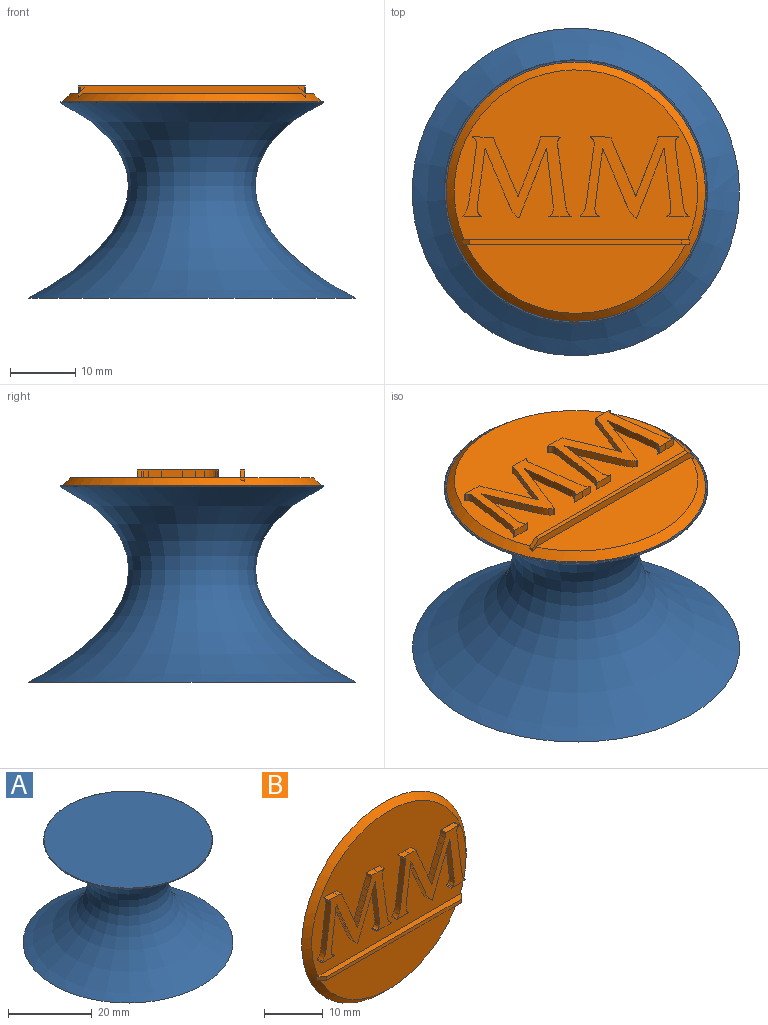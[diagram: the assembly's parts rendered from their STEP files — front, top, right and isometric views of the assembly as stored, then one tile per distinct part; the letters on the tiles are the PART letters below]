
ASSEMBLY  parts=2 mates=1
PART A: 4 faces, bbox 50x50x30 mm
  f0: plane 40.08x40.08mm, normal (0,0,1), area 1261.5mm2, adj f1
  f1: torus R=20.04mm, axis (0,0,1), area 34.2mm2, adj f0
  f2: plane 50x50mm, normal (0,0,-1), area 1963.5mm2, adj f3
  f3: revolved ~50x50mm, area 7734.9mm2, adj f2
PART B: 167 faces, bbox 39.6x2.4x39.6 mm
  f0: plane 37.2x25.95mm, normal (0,-1,0), area 657.2mm2, adj f3,f4,f5,f6,f7,f8,f9,f10
  f1: plane 33.53x10.54mm, normal (0,-1,0), area 253.3mm2, adj f160,f164
  f2: plane 39.6x39.6mm, normal (0,1,0), area 1231.6mm2, adj f164
  f3: plane 1.2x0.09mm, normal (0.59,0,-0.81), area 0.1mm2, adj f0,f4,f88,f89
  f4: extruded ~1.2x0.21mm, area 0.3mm2, adj f0,f3,f5,f89
  f5: extruded ~1.2x1.18mm, area 1.5mm2, adj f0,f4,f6,f89
  f6: extruded ~1.22x1.2mm, area 1.6mm2, adj f0,f5,f7,f89
  f7: extruded ~1.2x0.87mm, area 1.1mm2, adj f0,f6,f8,f89
  f8: extruded ~1.2x1mm, area 1.3mm2, adj f0,f7,f9,f89
  f9: extruded ~1.21x1.2mm, area 1.6mm2, adj f0,f8,f10,f89
  f10: extruded ~2.99x1.2mm, area 3.8mm2, adj f0,f9,f11,f89
  f11: extruded ~1.88x1.2mm, area 2.4mm2, adj f0,f10,f12,f89
  f12: extruded ~1.2x0.66mm, area 0.8mm2, adj f0,f11,f13,f89
  f13: extruded ~4.57x1.2mm, area 5.5mm2, adj f0,f12,f14,f89
  f14: extruded ~2.05x1.2mm, area 2.5mm2, adj f0,f13,f15,f89
  f15: extruded ~1.2x0.98mm, area 1.2mm2, adj f0,f14,f16,f89
  f16: extruded ~1.22x1.2mm, area 1.5mm2, adj f0,f15,f17,f89
  f17: extruded ~1.2x0.87mm, area 1.3mm2, adj f0,f16,f18,f89
  f18: extruded ~1.2x0.16mm, area 0.2mm2, adj f0,f17,f19,f89
  f19: extruded ~1.76x1.2mm, area 2.1mm2, adj f0,f18,f20,f89
  f20: extruded ~1.77x1.2mm, area 2.1mm2, adj f0,f19,f21,f89
  f21: extruded ~1.2x0.12mm, area 0.2mm2, adj f0,f20,f22,f89
  f22: extruded ~1.2x0.76mm, area 1.2mm2, adj f0,f21,f23,f89
  f23: extruded ~1.84x1.2mm, area 2.3mm2, adj f0,f22,f24,f89
  f24: extruded ~3.15x1.2mm, area 3.8mm2, adj f0,f23,f25,f89
  f25: extruded ~1.47x1.2mm, area 1.8mm2, adj f0,f24,f26,f89
  f26: extruded ~1.34x1.2mm, area 1.6mm2, adj f0,f25,f27,f89
  f27: extruded ~1.34x1.2mm, area 1.6mm2, adj f0,f26,f28,f89
  f28: extruded ~1.25x1.2mm, area 1.5mm2, adj f0,f27,f29,f89
  f29: extruded ~1.2x0.56mm, area 0.7mm2, adj f0,f28,f30,f89
  f30: extruded ~1.2x0.36mm, area 0.6mm2, adj f0,f29,f31,f89
  f31: plane 1.47x1.2mm, normal (0.03,0,1), area 1.8mm2, adj f0,f30,f32,f89
  f32: extruded ~1.59x1.2mm, area 1.9mm2, adj f0,f31,f33,f89
  f33: extruded ~1.2x0.17mm, area 0.2mm2, adj f0,f32,f34,f89
  f34: extruded ~2.01x1.2mm, area 2.6mm2, adj f0,f33,f35,f89
  f35: extruded ~1.2x0.5mm, area 0.6mm2, adj f0,f34,f36,f89
  f36: extruded ~1.2x1.15mm, area 1.5mm2, adj f0,f35,f37,f89
  f37: extruded ~1.2x0.88mm, area 1.1mm2, adj f0,f36,f38,f89
  f38: extruded ~1.2x1.18mm, area 1.5mm2, adj f0,f37,f39,f89
  f39: extruded ~1.2x0.67mm, area 0.9mm2, adj f0,f38,f40,f89
  f40: extruded ~1.2x0.67mm, area 0.9mm2, adj f0,f39,f41,f89
  f41: extruded ~1.2x1.04mm, area 1.3mm2, adj f0,f40,f42,f89
  f42: extruded ~1.2x0.8mm, area 1mm2, adj f0,f41,f43,f89
  f43: extruded ~1.2x0.03mm, area 0mm2, adj f0,f42,f44,f89
  f44: extruded ~1.2x1.14mm, area 1.5mm2, adj f0,f43,f45,f89
  f45: extruded ~2.86x1.22mm, area 3.7mm2, adj f0,f44,f46,f89
  f46: extruded ~1.2x1.15mm, area 1.5mm2, adj f0,f45,f47,f89
  f47: extruded ~1.2x0.43mm, area 0.6mm2, adj f0,f46,f48,f89
  f48: extruded ~1.2x0.72mm, area 0.9mm2, adj f0,f47,f49,f89
  f49: extruded ~1.31x1.2mm, area 1.7mm2, adj f0,f48,f50,f89
  f50: extruded ~1.3x1.2mm, area 1.7mm2, adj f0,f49,f51,f89
  f51: plane 1.2x0.97mm, normal (0.09,0,1), area 1.2mm2, adj f0,f50,f52,f89
  f52: plane 2.23x1.2mm, normal (0.02,0,1), area 2.7mm2, adj f0,f51,f53,f89
  f53: extruded ~1.2x0.01mm, area 0mm2, adj f0,f52,f54,f89
  f54: extruded ~1.2x0.11mm, area 0.2mm2, adj f0,f53,f55,f89
  f55: extruded ~1.2x0.57mm, area 0.9mm2, adj f0,f54,f56,f89
  f56: extruded ~1.2x0.36mm, area 0.4mm2, adj f0,f55,f57,f89
  f57: extruded ~1.2x0.63mm, area 0.8mm2, adj f0,f56,f58,f89
  f58: extruded ~2.05x1.2mm, area 2.5mm2, adj f0,f57,f59,f89
  f59: extruded ~3.18x1.2mm, area 3.8mm2, adj f0,f58,f60,f89
  f60: extruded ~1.98x1.2mm, area 2.4mm2, adj f0,f59,f61,f89
  f61: extruded ~1.46x1.2mm, area 1.8mm2, adj f0,f60,f62,f89
  f62: extruded ~1.72x1.2mm, area 2.3mm2, adj f0,f61,f63,f89
  f63: extruded ~1.2x0.17mm, area 0.3mm2, adj f0,f62,f64,f89
  f64: extruded ~1.2x0.26mm, area 0.3mm2, adj f0,f63,f65,f89
  f65: plane 2.71x1.2mm, normal (0,0,-1), area 3.3mm2, adj f0,f64,f66,f89
  f66: extruded ~1.2x0.01mm, area 0mm2, adj f0,f65,f67,f89
  f67: extruded ~1.2x0.02mm, area 0mm2, adj f0,f66,f68,f89
  f68: extruded ~1.2x0.3mm, area 0.4mm2, adj f0,f67,f69,f89
  f69: extruded ~1.2x0.62mm, area 0.9mm2, adj f0,f68,f70,f89
  f70: extruded ~1.2x1.02mm, area 1.2mm2, adj f0,f69,f71,f89
  f71: extruded ~1.4x1.2mm, area 1.7mm2, adj f0,f70,f72,f89
  f72: extruded ~2.1x1.2mm, area 2.5mm2, adj f0,f71,f73,f89
  f73: extruded ~1.82x1.2mm, area 2.2mm2, adj f0,f72,f74,f89
  f74: extruded ~1.62x1.2mm, area 2mm2, adj f0,f73,f75,f89
  f75: extruded ~1.59x1.2mm, area 1.9mm2, adj f0,f74,f76,f89
  f76: extruded ~1.2x0.04mm, area 0.1mm2, adj f0,f75,f77,f89
  f77: extruded ~1.2x1.12mm, area 1.5mm2, adj f0,f76,f78,f89
  f78: extruded ~1.48x1.2mm, area 1.9mm2, adj f0,f77,f79,f89
  f79: extruded ~1.2x0.67mm, area 0.9mm2, adj f0,f78,f80,f89
  f80: extruded ~1.2x1.02mm, area 1.3mm2, adj f0,f79,f81,f89
  f81: extruded ~1.2x1.03mm, area 1.3mm2, adj f0,f80,f82,f89
  f82: extruded ~1.2x0.39mm, area 0.5mm2, adj f0,f81,f83,f89
  f83: extruded ~1.2x0.33mm, area 0.4mm2, adj f0,f82,f84,f89
  f84: extruded ~1.2x0.74mm, area 1mm2, adj f0,f83,f85,f89
  f85: extruded ~1.2x0.79mm, area 1mm2, adj f0,f84,f86,f89
  f86: extruded ~2.34x1.2mm, area 3.2mm2, adj f0,f85,f87,f89
  f87: extruded ~1.2x0.56mm, area 0.9mm2, adj f0,f86,f88,f89
  f88: extruded ~1.2x0.13mm, area 0.2mm2, adj f0,f3,f87,f89
  f89: plane 16.69x12.41mm, normal (0,-1,0), area 76.1mm2, adj f3,f4,f5,f6,f7,f8,f9,f10
  f90: extruded ~1.2x0.15mm, area 0.2mm2, adj f0,f91,f157,f158
  f91: plane 1.2x0.27mm, normal (-0.03,0,-1), area 0.3mm2, adj f0,f90,f92,f158
  f92: extruded ~1.48x1.2mm, area 1.8mm2, adj f0,f91,f93,f158
  f93: extruded ~1.76x1.2mm, area 2.1mm2, adj f0,f92,f94,f158
  f94: extruded ~1.2x0.1mm, area 0.2mm2, adj f0,f93,f95,f158
  f95: extruded ~1.34x1.2mm, area 1.9mm2, adj f0,f94,f96,f158
  f96: extruded ~1.44x1.2mm, area 1.7mm2, adj f0,f95,f97,f158
  f97: extruded ~4.07x1.2mm, area 4.9mm2, adj f0,f96,f98,f158
  f98: extruded ~1.8x1.2mm, area 2.2mm2, adj f0,f97,f99,f158
  f99: extruded ~1.47x1.2mm, area 1.8mm2, adj f0,f98,f100,f158
  f100: extruded ~1.32x1.2mm, area 1.6mm2, adj f0,f99,f101,f158
  f101: extruded ~1.2x0.61mm, area 0.9mm2, adj f0,f100,f102,f158
  f102: extruded ~1.2x0.09mm, area 0.1mm2, adj f0,f101,f103,f158
  f103: extruded ~3.13x1.2mm, area 3.8mm2, adj f0,f102,f104,f158
  f104: extruded ~1.2x0.18mm, area 0.2mm2, adj f0,f103,f105,f158
  f105: extruded ~1.2x0.77mm, area 1mm2, adj f0,f104,f106,f158
  f106: extruded ~1.21x1.2mm, area 1.6mm2, adj f0,f105,f107,f158
  f107: extruded ~2.06x1.2mm, area 2.7mm2, adj f0,f106,f108,f158
  f108: extruded ~2.3x1.2mm, area 3mm2, adj f0,f107,f109,f158
  f109: extruded ~1.2x1.08mm, area 1.4mm2, adj f0,f108,f110,f158
  f110: extruded ~1.46x1.2mm, area 1.9mm2, adj f0,f109,f111,f158
  f111: extruded ~2.7x1.2mm, area 3.6mm2, adj f0,f110,f112,f158
  f112: extruded ~1.2x0.91mm, area 1.2mm2, adj f0,f111,f113,f158
  f113: extruded ~2.49x1.2mm, area 3.2mm2, adj f0,f112,f114,f158
  f114: extruded ~1.54x1.2mm, area 2mm2, adj f0,f113,f115,f158
  f115: extruded ~1.36x1.2mm, area 1.7mm2, adj f0,f114,f116,f158
  f116: plane 1.61x1.2mm, normal (0.06,0,1), area 1.9mm2, adj f0,f115,f117,f158
  f117: extruded ~1.59x1.2mm, area 1.9mm2, adj f0,f116,f118,f158
  f118: extruded ~1.2x0.11mm, area 0.2mm2, adj f0,f117,f119,f158
  f119: extruded ~1.2x0.42mm, area 0.7mm2, adj f0,f118,f120,f158
  f120: extruded ~1.2x1.07mm, area 1.3mm2, adj f0,f119,f121,f158
  f121: extruded ~1.2x1.04mm, area 1.3mm2, adj f0,f120,f122,f158
  f122: extruded ~3.1x1.2mm, area 3.7mm2, adj f0,f121,f123,f158
  f123: extruded ~1.2x0.86mm, area 1mm2, adj f0,f122,f124,f158
  f124: extruded ~1.2x0.73mm, area 0.9mm2, adj f0,f123,f125,f158
  f125: extruded ~2.06x1.2mm, area 2.5mm2, adj f0,f124,f126,f158
  f126: extruded ~2.07x1.2mm, area 2.6mm2, adj f0,f125,f127,f158
  f127: extruded ~1.2x0.65mm, area 1mm2, adj f0,f126,f128,f158
  f128: extruded ~1.2x0.14mm, area 0.2mm2, adj f0,f127,f129,f158
  f129: extruded ~1.2x0mm, area 0mm2, adj f0,f128,f130,f158
  f130: plane 2.96x1.2mm, normal (0,0,-1), area 3.5mm2, adj f0,f129,f131,f158
  f131: extruded ~1.2x0.01mm, area 0mm2, adj f0,f130,f132,f158
  f132: extruded ~1.2x0.07mm, area 0.1mm2, adj f0,f131,f133,f158
  f133: extruded ~1.2x0.37mm, area 0.6mm2, adj f0,f132,f134,f158
  f134: extruded ~1.51x1.2mm, area 1.9mm2, adj f0,f133,f135,f158
  f135: extruded ~3.35x1.2mm, area 4.1mm2, adj f0,f134,f136,f158
  f136: extruded ~2.24x1.2mm, area 2.7mm2, adj f0,f135,f137,f158
  f137: extruded ~2.97x1.2mm, area 3.6mm2, adj f0,f136,f138,f158
  f138: extruded ~1.2x0.87mm, area 1.1mm2, adj f0,f137,f139,f158
  f139: extruded ~1.25x1.2mm, area 1.6mm2, adj f0,f138,f140,f158
  f140: extruded ~2.88x1.21mm, area 3.7mm2, adj f0,f139,f141,f158
  f141: extruded ~4.32x1.86mm, area 5.6mm2, adj f0,f140,f142,f158
  f142: extruded ~1.2x1.15mm, area 1.8mm2, adj f0,f141,f143,f158
  f143: extruded ~1.2x0.21mm, area 0.3mm2, adj f0,f142,f144,f158
  f144: extruded ~1.2x0.75mm, area 1mm2, adj f0,f143,f145,f158
  f145: extruded ~2.09x1.2mm, area 2.7mm2, adj f0,f144,f146,f158
  f146: extruded ~1.56x1.2mm, area 2mm2, adj f0,f145,f147,f158
  f147: extruded ~1.69x1.2mm, area 2.2mm2, adj f0,f146,f148,f158
  f148: extruded ~1.2x0.61mm, area 0.8mm2, adj f0,f147,f149,f158
  f149: extruded ~1.2x1.15mm, area 1.5mm2, adj f0,f148,f150,f158
  f150: extruded ~2.61x1.2mm, area 3.4mm2, adj f0,f149,f151,f158
  f151: extruded ~1.2x0.16mm, area 0.2mm2, adj f0,f150,f152,f158
  f152: extruded ~1.41x1.2mm, area 1.7mm2, adj f0,f151,f153,f158
  f153: extruded ~2.78x1.2mm, area 3.4mm2, adj f0,f152,f154,f158
  f154: extruded ~2.66x1.2mm, area 3.2mm2, adj f0,f153,f155,f158
  f155: extruded ~1.67x1.2mm, area 2mm2, adj f0,f154,f156,f158
  f156: extruded ~1.63x1.2mm, area 2mm2, adj f0,f155,f157,f158
  f157: extruded ~1.2x0.26mm, area 0.4mm2, adj f0,f90,f156,f158
  f158: plane 16.68x12.45mm, normal (0,-1,0), area 76.3mm2, adj f90,f91,f92,f93,f94,f95,f96,f97
  f159: plane 0.72x0.57mm, normal (-1,0,0), area 0.3mm2, adj f160,f162,f164,f166
  f160: plane 34.76x1.76mm, normal (0,0,-1), area 40.6mm2, adj f1,f159,f161,f163,f164,f165,f166
  f161: plane 0.72x0.56mm, normal (1,0,0), area 0.3mm2, adj f160,f162,f164,f165
  f162: plane 34.76x1.47mm, normal (0,0,1), area 40.3mm2, adj f0,f159,f161,f163,f164,f165,f166
  f163: plane 32.36x0.71mm, normal (0,-1,0), area 22.9mm2, adj f160,f162,f165,f166
  f164: cone r=18.6mm half-angle=45deg, axis (0,1,0), area 203.8mm2, adj f0,f1,f2,f159,f160,f161,f162
  f165: plane 1.2x1.2mm, normal (0.71,-0.71,0), area 1.2mm2, adj f160,f161,f162,f163
  f166: plane 1.2x1.2mm, normal (-0.71,-0.71,0), area 1.2mm2, adj f159,f160,f162,f163
PLACE A at identity fixed
PLACE B rot(axis=(-1,0,0),90deg) t=(0,0,15)mm
MATE fastened A.f1 <-> B.f164  axis (0,0,1) through (0,0,15)mm
